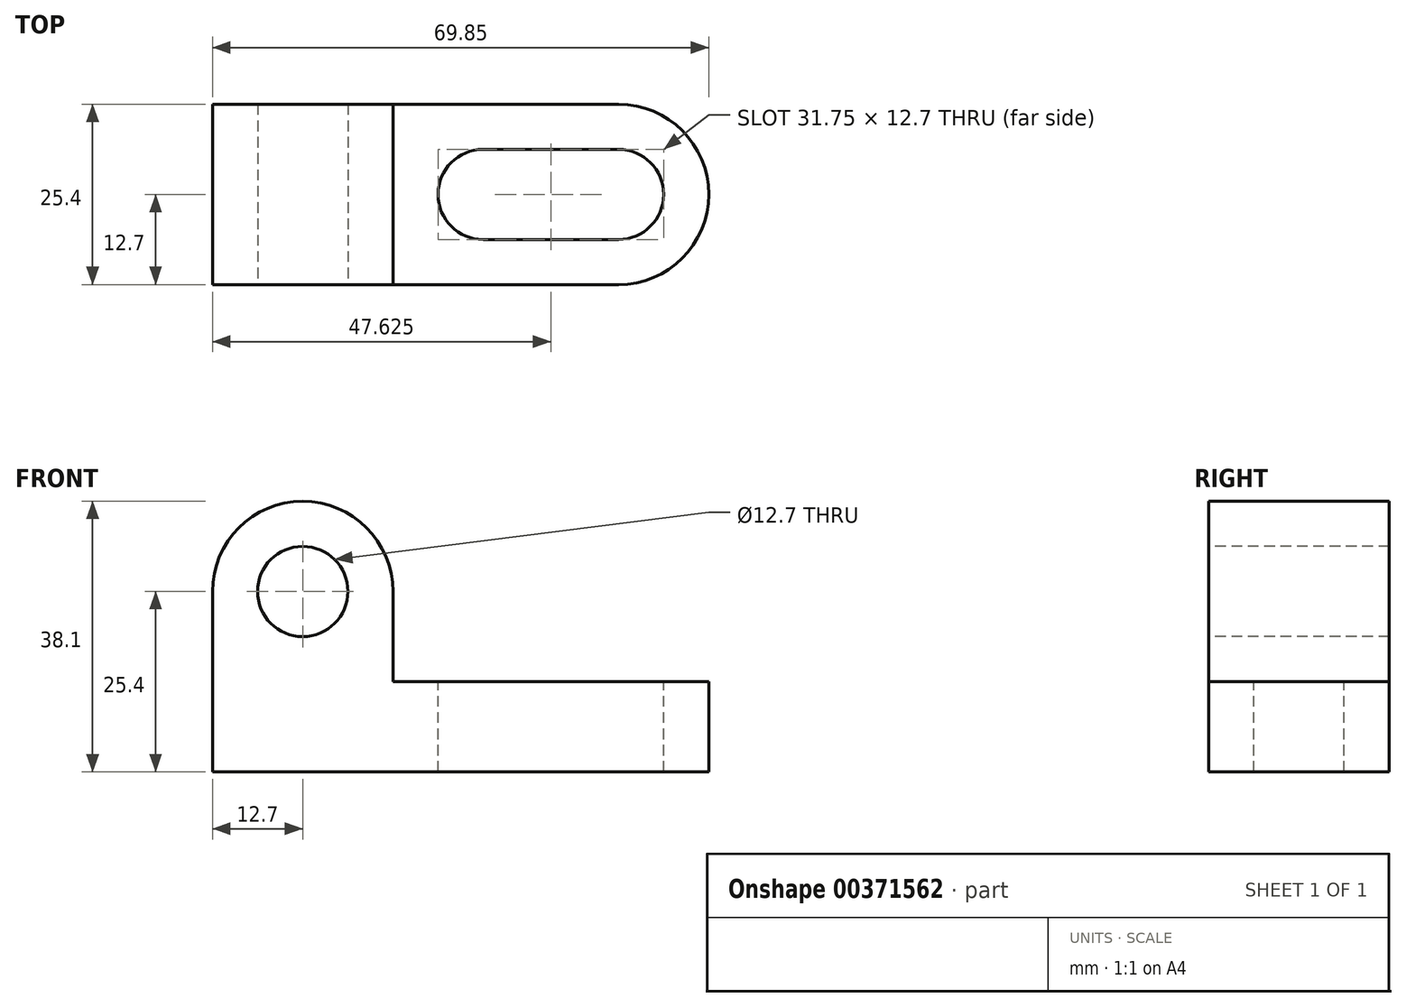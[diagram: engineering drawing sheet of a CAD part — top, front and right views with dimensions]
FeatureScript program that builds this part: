
annotation { "Feature Type Name" : "Feature", "Feature Type Description" : "" }
export const myFeature = defineFeature(function(context is Context, id is Id, definition is map)
    precondition{}
    {
        {
            var Q0;
            Q0=qCreatedBy(makeId("Front.planeOp"),FACE);
            var sketch = newSketch(context, id + "F0", { "sketchPlane" : qUnion([Q0])});
            skLineSegment(sketch, "E0", {"start": v(0, 0) * mm, "end": v(69.85, 0) * mm});
            skLineSegment(sketch, "E1", {"start": v(69.85, 0) * mm, "end": v(69.85, 12.7) * mm});
            skLineSegment(sketch, "E2", {"start": v(69.85, 12.7) * mm, "end": v(25.4, 12.7) * mm});
            skLineSegment(sketch, "E3", {"start": v(25.4, 12.7) * mm, "end": v(25.4, 38.1) * mm});
            skLineSegment(sketch, "E4", {"start": v(25.4, 38.1) * mm, "end": v(0, 38.1) * mm});
            skLineSegment(sketch, "E5", {"start": v(0, 38.1) * mm, "end": v(0, 0) * mm});
            skSolve(sketch);
        }
        {
            var Q0;
            Q0=makeQuery(id+"F0.imprint","IMPRINT",FACE,{"disambiguationData":[TD([[makeQuery(id+"F0.imprint","IMPRINT",EDGE,{"derivedFrom":sQuery(id+"F0.wireOp",EDGE,"E0")}),1.0]])]});
            extrude(context, id + "F1", {"entities" : qUnion([Q0]), "depth" : 25.4 * mm});
        }
        {
            var Q0;
            Q0=makeQuery(id+"F1.opExtrude","CAP_FACE",FACE,{"disambiguationData":[OSD([sQuery(id+"F0.wireOp",EDGE,"E0"),sQuery(id+"F0.wireOp",EDGE,"E1"),sQuery(id+"F0.wireOp",EDGE,"E2"),sQuery(id+"F0.wireOp",EDGE,"E3"),sQuery(id+"F0.wireOp",EDGE,"E4"),sQuery(id+"F0.wireOp",EDGE,"E5")])],"isStart":false});
            var sketch = newSketch(context, id + "F2", { "sketchPlane" : qUnion([Q0])});
            skCircle(sketch, "E6", {"center": v(12.7, 25.4) * mm, "radius": 6.35 * mm});
            skPoint(sketch, "E6.centerSnap0", {"position": v(12.7, 38.1) * mm});
            skArc(sketch, "E7", {"start": v(25.4, 25.4) * mm, "mid": v(12.7, 38.1) * mm, "end": v(0, 25.4) * mm});
            skSolve(sketch);
        }
        {
            var Q0;
            Q0=makeQuery(id+"F2.imprint","IMPRINT",FACE,{"disambiguationData":[TD([[makeQuery(id+"F2.imprint","IMPRINT",EDGE,{"derivedFrom":sQuery(id+"F2.wireOp",EDGE,"E6")}),1.0]])]});
            var Q1;
            {var subQ0=sQuery(id+"F2.wireOp",EDGE,"E7");var subQ1=makeQuery(id+"F1.opExtrude","CAP_EDGE",EDGE,{"disambiguationData":[OSD([sQuery(id+"F0.wireOp",EDGE,"E5")])],"isStart":false});var subQ2=makeQuery(id+"F2.imprint","INTERSECT",VERTEX,{"derivedFrom":[subQ1,subQ0]});Q1=makeQuery(id+"F2.imprint","IMPRINT",FACE,{"disambiguationData":[TD([[makeQuery(id+"F2.imprint","IMPRINT",EDGE,{"disambiguationData":[TD([[subQ2,1.0]])],"derivedFrom":subQ0}),-1.0]])]});}
            var Q2;
            {var subQ0=sQuery(id+"F2.wireOp",EDGE,"E7");var subQ1=makeQuery(id+"F1.opExtrude","CAP_EDGE",EDGE,{"disambiguationData":[OSD([sQuery(id+"F0.wireOp",EDGE,"E3")])],"isStart":false});var subQ2=makeQuery(id+"F2.imprint","INTERSECT",VERTEX,{"derivedFrom":[subQ1,subQ0]});Q2=makeQuery(id+"F2.imprint","IMPRINT",FACE,{"disambiguationData":[TD([[makeQuery(id+"F2.imprint","IMPRINT",EDGE,{"disambiguationData":[TD([[subQ2,-1.0]])],"derivedFrom":subQ0}),-1.0]])]});}
            extrude(context, id + "F3", {"entities" : qUnion([Q0, Q1, Q2]), "operationType" : NewBodyOperationType.REMOVE, "oppositeDirection" : true, "depth" : 25.4 * mm});
        }
        {
            var Q0;
            Q0=makeQuery(id+"F1.opExtrude","SWEPT_FACE",FACE,{"disambiguationData":[OSD([sQuery(id+"F0.wireOp",EDGE,"E2")])]});
            var sketch = newSketch(context, id + "F4", { "sketchPlane" : qUnion([Q0])});
            skCircle(sketch, "E8", {"center": v(38.1, -12.7) * mm, "radius": 6.35 * mm});
            skPoint(sketch, "E8.centerSnap0", {"position": v(25.4, -12.7) * mm});
            skCircle(sketch, "E9", {"center": v(57.15, -12.7) * mm, "radius": 6.35 * mm});
            skPoint(sketch, "E9.centerSnap0", {"position": v(69.85, -12.7) * mm});
            skLineSegment(sketch, "E10", {"start": v(38.1, -6.35) * mm, "end": v(57.15, -6.35) * mm});
            skLineSegment(sketch, "E11", {"start": v(38.1, -19.05) * mm, "end": v(57.15, -19.05) * mm});
            skArc(sketch, "E12", {"start": v(57.15, -25.4) * mm, "mid": v(69.85, -12.7) * mm, "end": v(57.15, 0) * mm});
            skSolve(sketch);
        }
        {
            var Q0;
            {var subQ0=sQuery(id+"F4.wireOp",EDGE,"E8");var subQ1=makeQuery(id+"F4.imprint","INTERSECT",VERTEX,{"derivedFrom":[subQ0,sQuery(id+"F4.wireOp",EDGE,"E10")]});Q0=makeQuery(id+"F4.imprint","IMPRINT",FACE,{"disambiguationData":[TD([[makeQuery(id+"F4.imprint","IMPRINT",EDGE,{"disambiguationData":[TD([[subQ1,-1.0]])],"derivedFrom":subQ0}),1.0]])]});}
            var Q1;
            {var subQ0=sQuery(id+"F4.wireOp",EDGE,"E10");Q1=makeQuery(id+"F4.imprint","IMPRINT",FACE,{"disambiguationData":[TD([[makeQuery(id+"F4.imprint","IMPRINT",EDGE,{"derivedFrom":subQ0}),-1.0]])]});}
            var Q2;
            {var subQ0=sQuery(id+"F4.wireOp",EDGE,"E9");var subQ1=makeQuery(id+"F4.imprint","INTERSECT",VERTEX,{"derivedFrom":[subQ0,sQuery(id+"F4.wireOp",EDGE,"E10")]});Q2=makeQuery(id+"F4.imprint","IMPRINT",FACE,{"disambiguationData":[TD([[makeQuery(id+"F4.imprint","IMPRINT",EDGE,{"disambiguationData":[TD([[subQ1,-1.0]])],"derivedFrom":subQ0}),1.0]])]});}
            var Q3;
            {var subQ0=sQuery(id+"F4.wireOp",EDGE,"E12");var subQ1=sQuery(id+"F0.wireOp",EDGE,"E2");var subQ2=makeQuery(id+"F1.opExtrude","CAP_EDGE",EDGE,{"disambiguationData":[OSD([subQ1])],"isStart":true});var subQ3=makeQuery(id+"F4.imprint","INTERSECT",VERTEX,{"derivedFrom":[subQ2,subQ0]});Q3=makeQuery(id+"F4.imprint","IMPRINT",FACE,{"disambiguationData":[TD([[makeQuery(id+"F4.imprint","IMPRINT",EDGE,{"disambiguationData":[TD([[subQ3,1.0]])],"derivedFrom":subQ0}),-1.0]])]});}
            var Q4;
            {var subQ0=sQuery(id+"F4.wireOp",EDGE,"E12");var subQ1=sQuery(id+"F0.wireOp",EDGE,"E2");var subQ2=makeQuery(id+"F1.opExtrude","CAP_EDGE",EDGE,{"disambiguationData":[OSD([subQ1])],"isStart":false});var subQ3=makeQuery(id+"F4.imprint","INTERSECT",VERTEX,{"derivedFrom":[subQ2,subQ0]});Q4=makeQuery(id+"F4.imprint","IMPRINT",FACE,{"disambiguationData":[TD([[makeQuery(id+"F4.imprint","IMPRINT",EDGE,{"disambiguationData":[TD([[subQ3,-1.0]])],"derivedFrom":subQ0}),-1.0]])]});}
            extrude(context, id + "F5", {"entities" : qUnion([Q0, Q1, Q2, Q3, Q4]), "operationType" : NewBodyOperationType.REMOVE, "oppositeDirection" : true, "depth" : 25.4 * mm});
        }
    });
